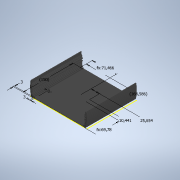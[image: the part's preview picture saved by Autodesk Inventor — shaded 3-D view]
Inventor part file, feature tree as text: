
AUTODESK INVENTOR PART (.ipt)
format: ipt  version: 2022 (Build 260153000, 153)  size: 433,152 bytes
history: native  units: mm
features: other x5, sketch x1, reference x1
ambient origin geometry x8: Origin, YZ Plane, XZ Plane, XY Plane, X Axis, Y Axis, Z Axis, Center Point
bodies: Solid1 (feature_tree), Volumenkörper1 (feature_tree)
feature tree (7):
  sketch  "Sketch1"  dims[d0=0.0mm d1=3.0mm d2=3.0mm d3=10.440924mm d4=69.779538mm d5=150.0mm d6=25.654376mm d7=168.586321mm d8=71.465973mm]
  reference  "Reference1"
  other  "<userpath>\Google Drive\Unicorn 2020\CAD_V2\Main_Assembly.iam"
  other  "Main_Assembly.iam"
  other  "Front_Panel_Assembly:1"
  other  "Front_Pane_Basel_Assembly:1"
  other  "DI 1600:1"
